# Revit family: Haworth_Immerse_SingleTable_RectangleOnePieceTop_120w
name_source: partatom
category: Furniture Systems
revit_build: Autodesk Revit 2018 (Build: 20170223_1515(x64)
units: mm (PartAtom-declared; Revit-internal decimal feet)

## family parameters
Always vertical = Yes
Cut with Voids When Loaded = No
OmniClass Number = 23.40.70.14.64.21
OmniClass Title = Systems Furniture
Part Type = Normal
Room Calculation Point = No
Round Connector Dimension = Use Diameter
Shared = No
Work Plane-Based = No

## types (3) — shared parameters
Actual Depth = 60"
Actual Width = 120"
Assembly Code = E2020200
Lower Top Cutout Depth = 12 1/2"
Lower Top Cutout Width = 78"
Lower Top Thickness = 1/8"
Lower Top Width = 118"
Manufacturer = Haworth
Model = THRA-60C0
Oblong Planter = Yes
Oblong Planter Void Height = 36"
Revision Number = 1
Size = Verify Final Dim. w/ Haworth
Standard Depths = 48, 60 in.
Standard Heights = 29, 36, 39 in.
Standard Widths = 96, 120 in.
URL = https://www.haworth.com
URL - Product = http://www.haworth.com
Understructure Overall Width = 81"
Understucture Thickness = 3 1/2"
Upper Top Thickness = 1 3/16"
Warranty = http://www.haworth.com

## per-type parameters (varying)
| type | Actual Height | Description |
| 60d 120w 39h - Oblong Planter | 39" | Haworth Immerse Single Table Rectangle One Piece Top - 60d 120w 39h - Oblong Planter |
| 60d 120w 36h - Oblong Planter | 36" | Haworth Immerse Single Table Rectangle One Piece Top - 60d 120w 36h - Oblong Planter |
| 60d 120w 29h - Oblong Planter | 29" | Haworth Immerse Single Table Rectangle One Piece Top - 60d 120w 29h - Oblong Planter |

## geometry (parser evidence)
native form markers: Sweep x8
no freeform markers — native parametric forms only
